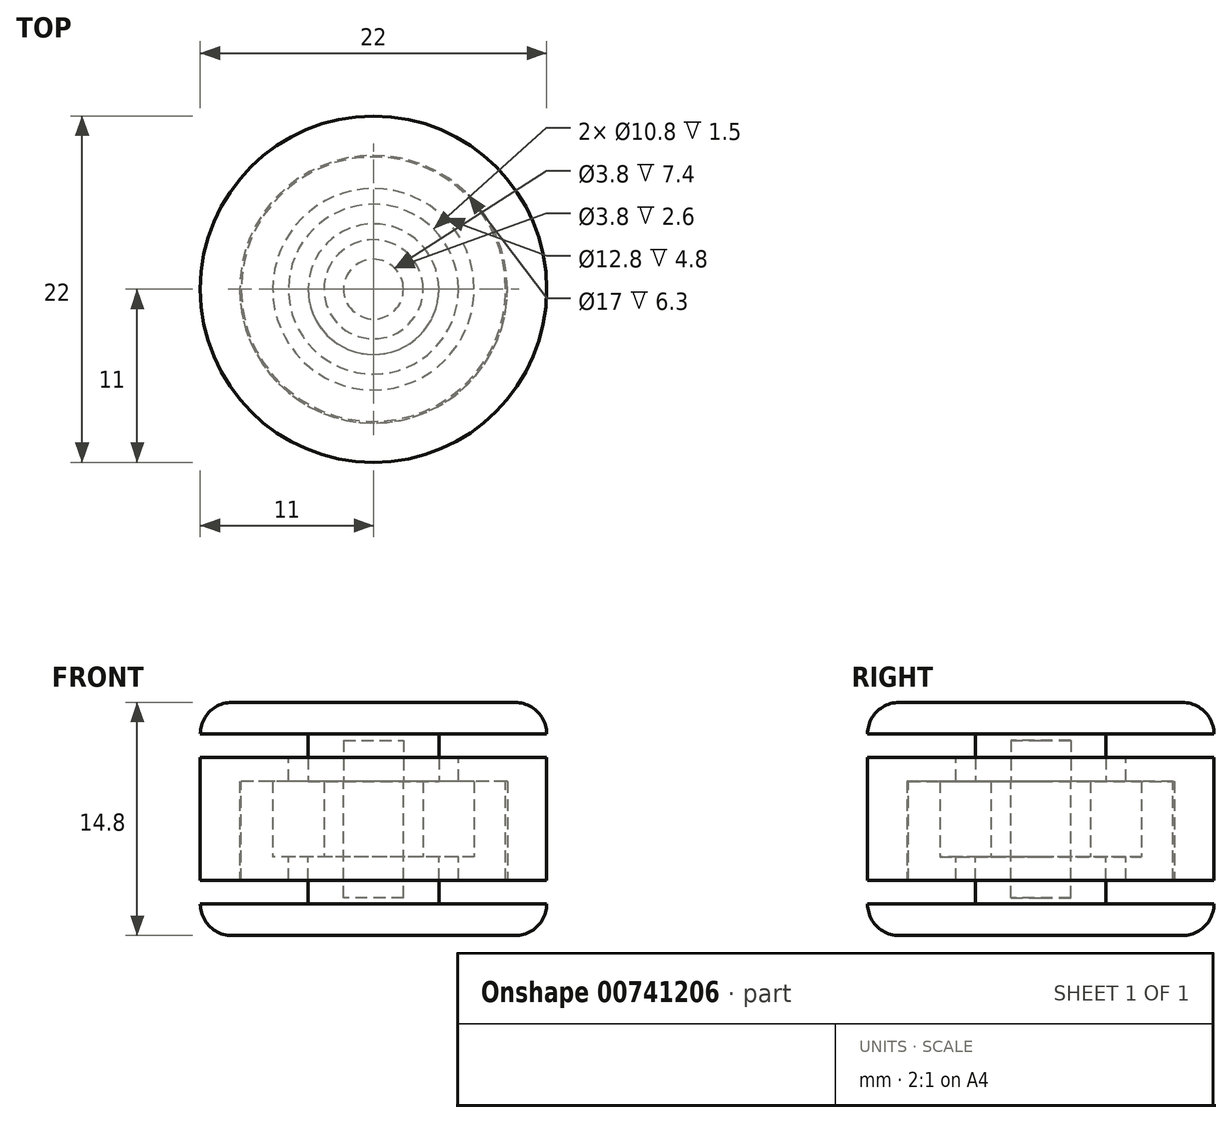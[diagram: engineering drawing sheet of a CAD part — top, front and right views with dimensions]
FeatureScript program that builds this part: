
annotation { "Feature Type Name" : "Feature", "Feature Type Description" : "" }
export const myFeature = defineFeature(function(context is Context, id is Id, definition is map)
    precondition{}
    {
        {
            var Q0;
            Q0=qCreatedBy(makeId("Top.planeOp"),FACE);
            var sketch = newSketch(context, id + "F0", { "sketchPlane" : qUnion([Q0])});
            skCircle(sketch, "E0", {"center": v(0, 0) * mm, "radius": 6.4 * mm, "construction": true});
            skArc(sketch, "E1", {"start": v(-2.5, 8.02) * mm, "mid": v(-7.27, 4.2) * mm, "end": v(-8.2, -1.84) * mm});
            skArc(sketch, "E2.trimOffspring", {"start": v(-5.7, -6.18) * mm, "mid": v(0, -8.4) * mm, "end": v(5.7, -6.18) * mm});
            skArc(sketch, "E3.trimOffspring", {"start": v(8.2, -1.84) * mm, "mid": v(7.27, 4.2) * mm, "end": v(2.5, 8.02) * mm});
            skCircle(sketch, "E4", {"center": v(0, 0) * mm, "radius": 5.4 * mm});
            skArc(sketch, "E5", {"start": v(-8.2, -1.84) * mm, "mid": v(-7.27, -4.2) * mm, "end": v(-5.7, -6.18) * mm});
            skArc(sketch, "E6.1.0", {"start": v(5.7, -6.18) * mm, "mid": v(7.27, -4.2) * mm, "end": v(8.2, -1.84) * mm});
            skArc(sketch, "E6.2.0", {"start": v(2.5, 8.02) * mm, "mid": v(0, 8.4) * mm, "end": v(-2.5, 8.02) * mm});
            skSolve(sketch);
        }
        {
            var Q0;
            Q0=qSketchRegion(id+"F0",true);
            extrude(context, id + "F1", {"entities" : qUnion([Q0]), "oppositeDirection" : true, "depth" : 1.5 * mm, "offsetDistance" : 25 * mm});
        }
        {
            var Q0;
            Q0=makeQuery(id+"F1.opExtrude","CAP_FACE",FACE,{"disambiguationData":[OSD([sQuery(id+"F0.wireOp",EDGE,"E1"),sQuery(id+"F0.wireOp",EDGE,"SSWOktfi-YVVa-QOHR-F3Zq-idvxaVufSt2G"),sQuery(id+"F0.wireOp",EDGE,"GNwKbPRx-9fyJ-GdU7-522C-Fg90mcq6ImYq"),sQuery(id+"F0.wireOp",EDGE,"ZGwsMqPZ-x5l7-tF8J-Zysn-qUefJ0FOqCIN"),sQuery(id+"F0.wireOp",EDGE,"VsKY3OOb-Xtje-pwYV-WHsk-dMj8n5GwY9Pl"),sQuery(id+"F0.wireOp",EDGE,"741e9558-03cd-4b54-b070-b39616ad76ed.1.0"),sQuery(id+"F0.wireOp",EDGE,"741e9558-03cd-4b54-b070-b39616ad76ed.1.1"),sQuery(id+"F0.wireOp",EDGE,"741e9558-03cd-4b54-b070-b39616ad76ed.1.2"),sQuery(id+"F0.wireOp",EDGE,"741e9558-03cd-4b54-b070-b39616ad76ed.1.3"),sQuery(id+"F0.wireOp",EDGE,"741e9558-03cd-4b54-b070-b39616ad76ed.2.0"),sQuery(id+"F0.wireOp",EDGE,"741e9558-03cd-4b54-b070-b39616ad76ed.2.1"),sQuery(id+"F0.wireOp",EDGE,"741e9558-03cd-4b54-b070-b39616ad76ed.2.2"),sQuery(id+"F0.wireOp",EDGE,"741e9558-03cd-4b54-b070-b39616ad76ed.2.3"),sQuery(id+"F0.wireOp",EDGE,"E2.trimOffspring"),sQuery(id+"F0.wireOp",EDGE,"E3.trimOffspring"),sQuery(id+"F0.wireOp",EDGE,"E4")])],"isStart":true});
            var sketch = newSketch(context, id + "F2", { "sketchPlane" : qUnion([Q0])});
            skCircle(sketch, "E7", {"center": v(0, 0) * mm, "radius": 6.4 * mm});
            skCircle(sketch, "E8", {"center": v(0, 0) * mm, "radius": 8.4 * mm});
            skSolve(sketch);
        }
        {
            var Q0;
            Q0=qSketchRegion(id+"F2",true);
            extrude(context, id + "F3", {"entities" : qUnion([Q0]), "operationType" : NewBodyOperationType.ADD, "depth" : 4.8 * mm, "offsetDistance" : 25 * mm});
        }
        {
            var Q0;
            Q0=makeQuery(id+"F1.opExtrude","CAP_FACE",FACE,{"disambiguationData":[OSD([sQuery(id+"F0.wireOp",EDGE,"E1"),sQuery(id+"F0.wireOp",EDGE,"SSWOktfi-YVVa-QOHR-F3Zq-idvxaVufSt2G"),sQuery(id+"F0.wireOp",EDGE,"GNwKbPRx-9fyJ-GdU7-522C-Fg90mcq6ImYq"),sQuery(id+"F0.wireOp",EDGE,"ZGwsMqPZ-x5l7-tF8J-Zysn-qUefJ0FOqCIN"),sQuery(id+"F0.wireOp",EDGE,"VsKY3OOb-Xtje-pwYV-WHsk-dMj8n5GwY9Pl"),sQuery(id+"F0.wireOp",EDGE,"741e9558-03cd-4b54-b070-b39616ad76ed.1.0"),sQuery(id+"F0.wireOp",EDGE,"741e9558-03cd-4b54-b070-b39616ad76ed.1.1"),sQuery(id+"F0.wireOp",EDGE,"741e9558-03cd-4b54-b070-b39616ad76ed.1.2"),sQuery(id+"F0.wireOp",EDGE,"741e9558-03cd-4b54-b070-b39616ad76ed.1.3"),sQuery(id+"F0.wireOp",EDGE,"741e9558-03cd-4b54-b070-b39616ad76ed.2.0"),sQuery(id+"F0.wireOp",EDGE,"741e9558-03cd-4b54-b070-b39616ad76ed.2.1"),sQuery(id+"F0.wireOp",EDGE,"741e9558-03cd-4b54-b070-b39616ad76ed.2.2"),sQuery(id+"F0.wireOp",EDGE,"741e9558-03cd-4b54-b070-b39616ad76ed.2.3"),sQuery(id+"F0.wireOp",EDGE,"E2.trimOffspring"),sQuery(id+"F0.wireOp",EDGE,"E3.trimOffspring"),sQuery(id+"F0.wireOp",EDGE,"E4")])],"isStart":false});
            var sketch = newSketch(context, id + "F4", { "sketchPlane" : qUnion([Q0])});
            skCircle(sketch, "E9", {"center": v(0, 0) * mm, "radius": 11 * mm});
            skCircle(sketch, "E10", {"center": v(0, 0) * mm, "radius": 8.5 * mm});
            skSolve(sketch);
        }
        {
            var Q0;
            Q0=qSketchRegion(id+"F4",true);
            extrude(context, id + "F5", {"entities" : qUnion([Q0]), "oppositeDirection" : true, "depth" : (4.8 + 3) * mm, "offsetDistance" : 25 * mm});
        }
        {
            var Q0;
            Q0=makeQuery(id+"F5.opExtrude","CAP_FACE",FACE,{"disambiguationData":[OSD([sQuery(id+"F4.wireOp",EDGE,"E9"),sQuery(id+"F4.wireOp",EDGE,"E10"),sQuery(id+"F4.wireOp",EDGE,"afdc47bc-32eb-4de7-befb-8ba8e129a2fd.0"),sQuery(id+"F4.wireOp",EDGE,"afdc47bc-32eb-4de7-befb-8ba8e129a2fd.1"),sQuery(id+"F4.wireOp",EDGE,"afdc47bc-32eb-4de7-befb-8ba8e129a2fd.2"),sQuery(id+"F4.wireOp",EDGE,"97b018c1-320c-4275-b937-d7f2b59cc8b2.1.0"),sQuery(id+"F4.wireOp",EDGE,"97b018c1-320c-4275-b937-d7f2b59cc8b2.1.1"),sQuery(id+"F4.wireOp",EDGE,"97b018c1-320c-4275-b937-d7f2b59cc8b2.1.2"),sQuery(id+"F4.wireOp",EDGE,"97b018c1-320c-4275-b937-d7f2b59cc8b2.2.0"),sQuery(id+"F4.wireOp",EDGE,"97b018c1-320c-4275-b937-d7f2b59cc8b2.2.1"),sQuery(id+"F4.wireOp",EDGE,"97b018c1-320c-4275-b937-d7f2b59cc8b2.2.2")])],"isStart":false});
            var sketch = newSketch(context, id + "F6", { "sketchPlane" : qUnion([Q0])});
            skCircle(sketch, "E11", {"center": v(0, 0) * mm, "radius": 5.4 * mm});
            skCircle(sketch, "E12", {"center": v(0, 0) * mm, "radius": 11 * mm});
            skSolve(sketch);
        }
        {
            var Q0;
            Q0=qSketchRegion(id+"F6",true);
            extrude(context, id + "F7", {"entities" : qUnion([Q0]), "operationType" : NewBodyOperationType.ADD, "oppositeDirection" : true, "depth" : 1.5 * mm, "offsetDistance" : 25 * mm});
        }
        {
            var Q0;
            Q0=makeQuery(id+"F1.opExtrude","CAP_FACE",FACE,{"disambiguationData":[OSD([sQuery(id+"F0.wireOp",EDGE,"E1"),sQuery(id+"F0.wireOp",EDGE,"E2.trimOffspring"),sQuery(id+"F0.wireOp",EDGE,"E3.trimOffspring"),sQuery(id+"F0.wireOp",EDGE,"E4"),sQuery(id+"F0.wireOp",EDGE,"E5"),sQuery(id+"F0.wireOp",EDGE,"E6.1.0"),sQuery(id+"F0.wireOp",EDGE,"E6.2.0")])],"isStart":true});
            var sketch = newSketch(context, id + "F8", { "sketchPlane" : qUnion([Q0])});
            skCircle(sketch, "E13", {"center": v(0, 0) * mm, "radius": 3.15 * mm});
            skSolve(sketch);
        }
        {
            var Q0;
            Q0=qSketchRegion(id+"F8",true);
            extrude(context, id + "F9", {"entities" : qUnion([Q0]), "depth" : 4.8 * mm, "offsetDistance" : 25 * mm});
        }
        {
            var Q0;
            Q0=makeQuery(id+"F9.opExtrude","CAP_FACE",FACE,{"disambiguationData":[OSD([sQuery(id+"F8.wireOp",EDGE,"E13"),sQuery(id+"F8.wireOp",EDGE,"LKHf6wPm-FpDQ-OeeC-ccY9-ThEM7THS3bii")])],"isStart":true});
            var sketch = newSketch(context, id + "F10", { "sketchPlane" : qUnion([Q0])});
            skCircle(sketch, "E14", {"center": v(0, 0) * mm, "radius": 4.15 * mm});
            skSolve(sketch);
        }
        {
            var Q0;
            Q0=qSketchRegion(id+"F10",true);
            var Q1;
            Q1=makeQuery(id+"F1.opExtrude","CAP_FACE",FACE,{"disambiguationData":[OSD([sQuery(id+"F0.wireOp",EDGE,"E1"),sQuery(id+"F0.wireOp",EDGE,"E2.trimOffspring"),sQuery(id+"F0.wireOp",EDGE,"E3.trimOffspring"),sQuery(id+"F0.wireOp",EDGE,"E4"),sQuery(id+"F0.wireOp",EDGE,"E5"),sQuery(id+"F0.wireOp",EDGE,"E6.1.0"),sQuery(id+"F0.wireOp",EDGE,"E6.2.0")])],"isStart":false});
            extrude(context, id + "F11", {"entities" : qUnion([Q0]), "operationType" : NewBodyOperationType.ADD, "endBound" : BoundingType.UP_TO_SURFACE, "depth" : 25 * mm, "endBoundEntityFace" : qUnion([Q1]), "hasOffset" : true, "offsetDistance" : 1.5 * mm, "offsetOppositeDirection" : true});
        }
        {
            var Q0;
            Q0=makeQuery(id+"F11.opExtrude","CAP_FACE",FACE,{"disambiguationData":[OSD([sQuery(id+"F10.wireOp",EDGE,"E14")])],"isStart":false});
            var sketch = newSketch(context, id + "F12", { "sketchPlane" : qUnion([Q0])});
            skCircle(sketch, "E15", {"center": v(0, 0) * mm, "radius": 11 * mm});
            skSolve(sketch);
        }
        {
            var Q0;
            Q0=qSketchRegion(id+"F12",true);
            extrude(context, id + "F13", {"entities" : qUnion([Q0]), "operationType" : NewBodyOperationType.ADD, "depth" : 2 * mm, "offsetDistance" : 25 * mm});
        }
        {
            var Q0;
            Q0=makeQuery(id+"F9.opExtrude","CAP_FACE",FACE,{"disambiguationData":[OSD([sQuery(id+"F8.wireOp",EDGE,"E13")])],"isStart":false});
            var sketch = newSketch(context, id + "F14", { "sketchPlane" : qUnion([Q0])});
            skCircle(sketch, "E16", {"center": v(0, 0) * mm, "radius": 1.9 * mm});
            skSolve(sketch);
        }
        {
            var Q0;
            Q0=qSketchRegion(id+"F14",true);
            extrude(context, id + "F15", {"entities" : qUnion([Q0]), "operationType" : NewBodyOperationType.REMOVE, "oppositeDirection" : true, "depth" : (2.4 + 5) * mm, "offsetDistance" : 25 * mm});
        }
        {
            var Q0;
            Q0=makeQuery(id+"F11.opExtrude","CAP_EDGE",EDGE,{"disambiguationData":[OSD([sQuery(id+"F10.wireOp",EDGE,"E14")])],"isStart":false});
            var Q1;
            Q1=makeQuery(id+"F13.opExtrude","CAP_EDGE",EDGE,{"disambiguationData":[OSD([sQuery(id+"F12.wireOp",EDGE,"E15")])],"isStart":false});
            fillet(context, id + "F16", {"entities" : qUnion([Q0, Q1]), "radius" : 2 * mm, "tangentPropagation" : true, "allowEdgeOverflow" : false});
        }
        {
            var Q0;
            Q0=makeQuery(id+"F9.opExtrude","CAP_FACE",FACE,{"disambiguationData":[OSD([sQuery(id+"F8.wireOp",EDGE,"E13")])],"isStart":false});
            var sketch = newSketch(context, id + "F17", { "sketchPlane" : qUnion([Q0])});
            skCircle(sketch, "E17.0", {"center": v(0, 0) * mm, "radius": 4.15 * mm});
            skSolve(sketch);
        }
        {
            var Q0;
            Q0=qSketchRegion(id+"F17",true);
            var Q1;
            Q1=makeQuery(id+"F7.boolean.opBoolean","MERGE",FACE,{"derivedFrom":[makeQuery(id+"F5.opExtrude","CAP_FACE",FACE,{"disambiguationData":[OSD([sQuery(id+"F4.wireOp",EDGE,"E9"),sQuery(id+"F4.wireOp",EDGE,"E10")])],"isStart":false}),makeQuery(id+"F7.opExtrude","CAP_FACE",FACE,{"disambiguationData":[OSD([sQuery(id+"F6.wireOp",EDGE,"E11"),sQuery(id+"F6.wireOp",EDGE,"E12")])],"isStart":true})]});
            extrude(context, id + "F18", {"entities" : qUnion([Q0]), "endBound" : BoundingType.UP_TO_SURFACE, "depth" : 25 * mm, "endBoundEntityFace" : qUnion([Q1]), "hasOffset" : true, "offsetDistance" : 1.5 * mm, "offsetOppositeDirection" : true});
        }
        {
            var Q0;
            Q0=makeQuery(id+"F18.opExtrude","CAP_FACE",FACE,{"disambiguationData":[OSD([sQuery(id+"F17.wireOp",EDGE,"E17.0")])],"isStart":false});
            var sketch = newSketch(context, id + "F19", { "sketchPlane" : qUnion([Q0])});
            skCircle(sketch, "E18.0", {"center": v(0, 0) * mm, "radius": 11 * mm});
            skSolve(sketch);
        }
        {
            var Q0;
            Q0=qSketchRegion(id+"F19",true);
            extrude(context, id + "F20", {"entities" : qUnion([Q0]), "operationType" : NewBodyOperationType.ADD, "depth" : 2 * mm, "offsetDistance" : 25 * mm});
        }
        {
            var Q0;
            Q0=makeQuery(id+"F18.opExtrude","CAP_FACE",FACE,{"disambiguationData":[OSD([sQuery(id+"F17.wireOp",EDGE,"E17.0")])],"isStart":true});
            var sketch = newSketch(context, id + "F21", { "sketchPlane" : qUnion([Q0])});
            skCircle(sketch, "E19.0", {"center": v(0, 0) * mm, "radius": 1.9 * mm});
            skSolve(sketch);
        }
        {
            var Q0;
            Q0=qSketchRegion(id+"F21",true);
            extrude(context, id + "F22", {"entities" : qUnion([Q0]), "operationType" : NewBodyOperationType.REMOVE, "oppositeDirection" : true, "depth" : (5 - 2.4) * mm, "offsetDistance" : 25 * mm});
        }
        {
            var Q0;
            Q0=makeQuery(id+"F20.opExtrude","CAP_EDGE",EDGE,{"disambiguationData":[OSD([sQuery(id+"F19.wireOp",EDGE,"E18.0")])],"isStart":false});
            var Q1;
            Q1=makeQuery(id+"F18.opExtrude","CAP_EDGE",EDGE,{"disambiguationData":[OSD([sQuery(id+"F17.wireOp",EDGE,"E17.0")])],"isStart":false});
            fillet(context, id + "F23", {"entities" : qUnion([Q0, Q1]), "radius" : 2 * mm, "tangentPropagation" : true, "allowEdgeOverflow" : false});
        }
    });
